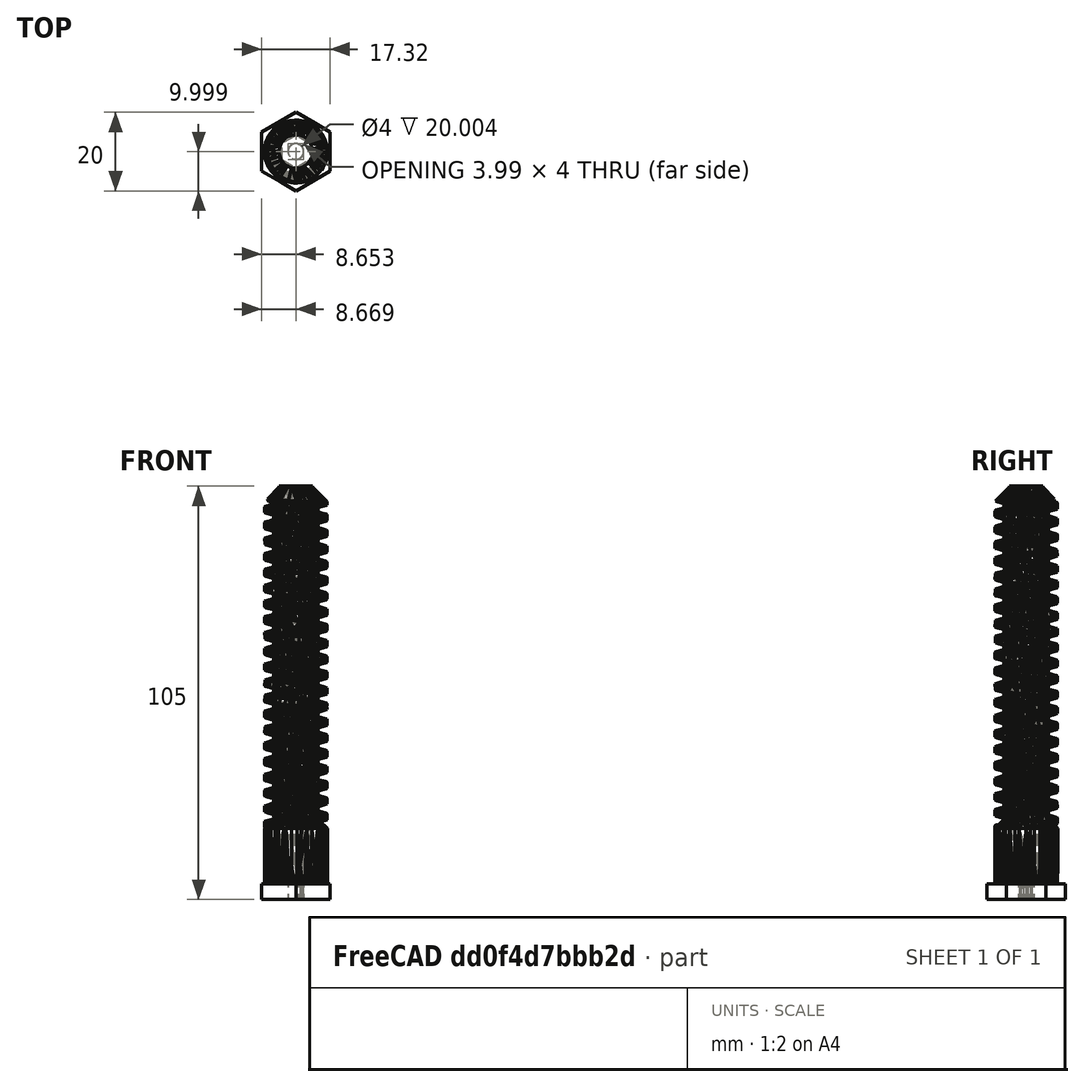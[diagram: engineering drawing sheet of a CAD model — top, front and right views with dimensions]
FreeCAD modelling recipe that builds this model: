
FCSTD DOCUMENT  (FreeCAD 1.0R39285 (Git))
Label: screw-repaired-mod
License: All rights reserved
LicenseURL: https://en.wikipedia.org/wiki/All_rights_reserved
objects: Part::Feature×2, Sketcher::SketchObject×2, Mesh::Feature×1, PartDesign::FeatureBase×1, PartDesign::Pad×1, PartDesign::Pocket×1, PartDesign::Body×1
note: 15 computed .brp shape members not serialized (recipe doc carries the construction recipe); baked Part::Feature solids carry a one-line shape summary decoded from their .brp

FEATURE [Mesh::Feature] screw_repaired  label="screw-repaired"
FEATURE [Part::Feature] screw_repaired001
  shape: bbox 17.32 x 20 x 105 mm, 7626 faces, 0 solids (baked)
FEATURE [Part::Feature] screw_repaired001_solid  label="screw_repaired001 (Solid)"
  shape: bbox 17.32 x 20 x 105 mm, 7626 faces (baked)
FEATURE [PartDesign::FeatureBase] BaseFeature
  BaseFeature = -> screw_repaired001_solid
  Suppressed = false
FEATURE [Sketcher::SketchObject] Sketch
  ArcFitTolerance = 1e-06
  AttachmentSupport = -> [BaseFeature]
  ExternalGeometry = -> [BaseFeature]
  FullyConstrained = true
  MakeInternals = false
  MapMode = 5
  Placement = pos=(0,0,104.997) rot=(0,0,1;0rad)
  sketch-geometry (3):
    g0: Circle [constr] CenterX=125 CenterY=104.999 CenterZ=0 NormalX=0 NormalY=0 NormalZ=1 AngleXU=0 Radius=2.002
    g1: Circle CenterX=125 CenterY=104.999 CenterZ=0 NormalX=0 NormalY=0 NormalZ=1 AngleXU=0 Radius=4.25
    g2: LineSegment [constr] StartX=125 StartY=104.999 StartZ=0 EndX=125 EndY=109.249 EndZ=0
  constraints (8):
    c: PointOnObject(g-10,g0)
    c: PointOnObject(g-12,g0)
    c: PointOnObject(g-11,g0)
    c: Coincident(g1,g0)
    c: Coincident(g2,g0)
    c: PointOnObject(g2,g1)
    c: Vertical(g2)
    c: DistanceY(g2,g2) = 4.25
FEATURE [PartDesign::Pad] Pad
  BaseFeature = -> BaseFeature
  Direction = (0,0,1)
  Length = 95
  Length2 = 10
  Profile = -> Sketch
  ReferenceAxis = -> Sketch [N_Axis]
  Refine = true
  Reversed = true
  Suppressed = false
  Type = 0
FEATURE [Sketcher::SketchObject] Sketch001
  ArcFitTolerance = 1e-06
  AttachmentSupport = -> [Pad]
  ExternalGeometry = -> [Pad]
  FullyConstrained = true
  MakeInternals = false
  MapMode = 5
  Placement = pos=(0,0,0.000499725) rot=(1,0,0;3.14159rad)
  sketch-geometry (1):
    g0: Circle CenterX=124.993 CenterY=-104.999 CenterZ=0 NormalX=0 NormalY=0 NormalZ=1 AngleXU=0 Radius=2.0021
  constraints (3):
    c: PointOnObject(g-3,g0)
    c: PointOnObject(g-3,g0)
    c: PointOnObject(g-4,g0)
FEATURE [PartDesign::Pocket] Pocket
  BaseFeature = -> Pad
  Direction = (0,0,1)
  Length = 30
  Length2 = 5
  Profile = -> Sketch001
  ReferenceAxis = -> Sketch001 [N_Axis]
  Refine = true
  Suppressed = false
  Type = 0
FEATURE [PartDesign::Body] Body
  AllowCompound = false
  BaseFeature = -> screw_repaired001_solid
  Group = -> [BaseFeature,Sketch,Pad,Sketch001,Pocket]
  Origin = -> Origin
  Tip = -> Pocket
